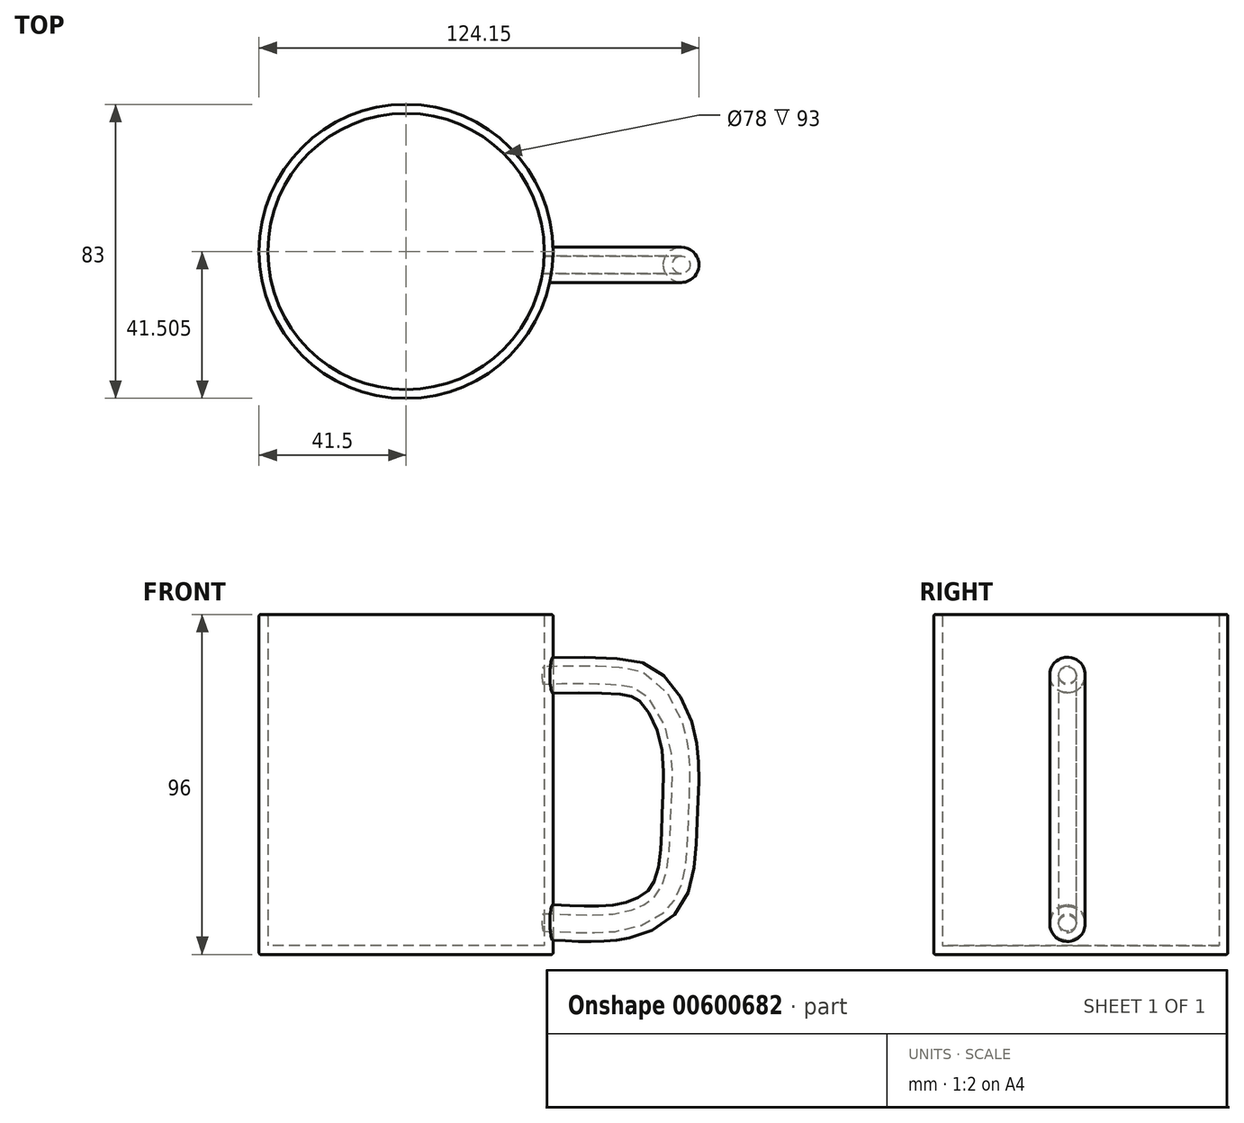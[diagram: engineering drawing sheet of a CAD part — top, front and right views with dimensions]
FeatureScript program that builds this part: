
annotation { "Feature Type Name" : "Feature", "Feature Type Description" : "" }
export const myFeature = defineFeature(function(context is Context, id is Id, definition is map)
    precondition{}
    {
        {
            var Q0;
            Q0=qCreatedBy(makeId("Top.planeOp"),FACE);
            var sketch = newSketch(context, id + "F0", { "sketchPlane" : qUnion([Q0])});
            skCircle(sketch, "E0", {"center": v(0, 3.76) * mm, "radius": 41.5 * mm});
            skSolve(sketch);
        }
        {
            var Q0;
            Q0=makeQuery(id+"F0.imprint","IMPRINT",FACE,{"disambiguationData":[TD([[makeQuery(id+"F0.imprint","IMPRINT",EDGE,{"derivedFrom":sQuery(id+"F0.wireOp",EDGE,"E0")}),1.0]])]});
            extrude(context, id + "F1", {"entities" : qUnion([Q0]), "depth" : 96 * mm, "offsetDistance" : 25 * mm});
        }
        {
            var Q0;
            Q0=qCreatedBy(makeId("Front.planeOp"),FACE);
            var sketch = newSketch(context, id + "F2", { "sketchPlane" : qUnion([Q0])});
            skFitSpline(sketch, "E1", {"points": [v(36.44, 78.72) * mm, v(59.32, 78.72) * mm, v(68.53, 75.99) * mm, v(76.73, 61.56) * mm, v(77.48, 41.91) * mm, v(76.98, 29.72) * mm, v(73.75, 16.54) * mm, v(65.3, 10.32) * mm, v(56.09, 8.58) * mm, v(47.38, 8.58) * mm, v(32.7, 8.83) * mm], "startDerivative": vector(209.6, 11.33) * mm, "endDerivative": vector(-216.96, -7.48) * mm});
            skSolve(sketch);
        }
        {
            var Q0;
            Q0=qCreatedBy(makeId("Right.planeOp"),FACE);
            cPlane(context, id + "F3", {"entities" : qUnion([Q0]), "cplaneType" : CPlaneType.OFFSET, "offset" : 41.5 * mm, "width" : 150 * mm, "height" : 150 * mm});
        }
        {
            var Q0;
            Q0=qCreatedBy(id+"F3.planeOp",FACE);
            var sketch = newSketch(context, id + "F4", { "sketchPlane" : qUnion([Q0])});
            skCircle(sketch, "E2", {"center": v(0, 78.8) * mm, "radius": 5 * mm});
            skSolve(sketch);
        }
        {
            var Q0;
            Q0=makeQuery(id+"F4.imprint","IMPRINT",FACE,{"disambiguationData":[TD([[makeQuery(id+"F4.imprint","IMPRINT",EDGE,{"derivedFrom":sQuery(id+"F4.wireOp",EDGE,"E2")}),1.0]])]});
            var Q1;
            Q1=sQuery(id+"F2.wireOp",EDGE,"E1");
            sweep(context, id + "F5", {"operationType" : NewBodyOperationType.ADD, "profiles" : qUnion([Q0]), "path" : qUnion([Q1])});
        }
        {
            var Q0;
            Q0=makeQuery(id+"F1.opExtrude","CAP_FACE",FACE,{"disambiguationData":[OSD([sQuery(id+"F0.wireOp",EDGE,"E0")])],"isStart":false});
            shell(context, id + "F6", {"entities" : qUnion([Q0]), "thickness" : 2.5 * mm});
        }
        {
            var Q0;
            {var subQ0=sQuery(id+"F0.wireOp",EDGE,"E0");Q0=makeQuery(id+"F6.opShell","OFFSET_EDGE",EDGE,{"disambiguationData":[OSD([subQ0]),TDD([makeQuery(id+"F1.opExtrude","CAP_EDGE",EDGE,{"disambiguationData":[OSD([subQ0])],"isStart":false})])]});}
            var Q1;
            Q1=makeQuery(id+"F1.opExtrude","CAP_EDGE",EDGE,{"disambiguationData":[OSD([sQuery(id+"F0.wireOp",EDGE,"E0")])],"isStart":false});
            var Q2;
            Q2=makeQuery(id+"F1.opExtrude","CAP_EDGE",EDGE,{"disambiguationData":[OSD([sQuery(id+"F0.wireOp",EDGE,"E0")])],"isStart":true});
            fillet(context, id + "F7", {"entities" : qUnion([Q0, Q1, Q2]), "radius" : 0.5 * mm, "tangentPropagation" : true, "allowEdgeOverflow" : false});
        }
    });
